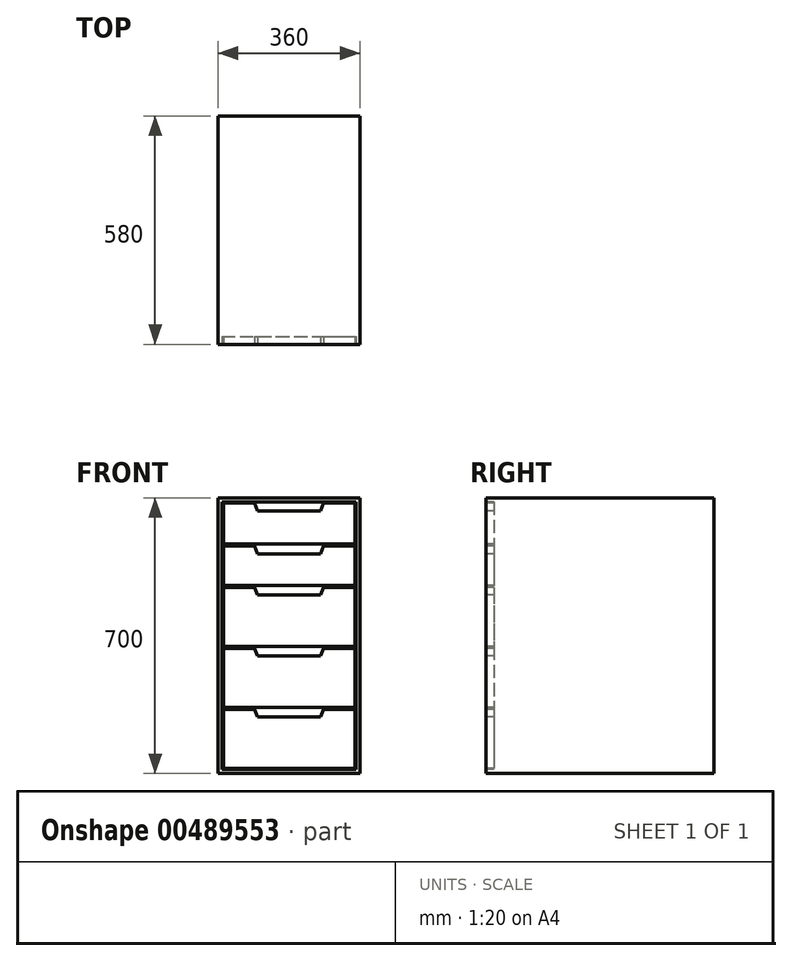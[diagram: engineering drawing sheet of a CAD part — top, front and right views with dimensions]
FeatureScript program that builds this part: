
annotation { "Feature Type Name" : "Feature", "Feature Type Description" : "" }
export const myFeature = defineFeature(function(context is Context, id is Id, definition is map)
    precondition{}
    {
        {
            var Q0;
            Q0=qCreatedBy(makeId("Top.planeOp"),FACE);
            var sketch = newSketch(context, id + "F0", { "sketchPlane" : qUnion([Q0])});
            skLineSegment(sketch, "E0.bottom", {"start": v(180, -290) * mm, "end": v(-180, -290) * mm});
            skLineSegment(sketch, "E0.top", {"start": v(180, 290) * mm, "end": v(-180, 290) * mm});
            skLineSegment(sketch, "E0.left", {"start": v(180, -290) * mm, "end": v(180, 290) * mm});
            skLineSegment(sketch, "E0.right", {"start": v(-180, -290) * mm, "end": v(-180, 290) * mm});
            skPoint(sketch, "E0.middle", {"position": v(0, 0) * mm});
            skSolve(sketch);
        }
        {
            var Q0;
            Q0 = qSketchRegion(id + "F0", true);
            extrude(context, id + "F1", {"entities" : qUnion([Q0]), "depth" : 700 * mm});
        }
        {
            var Q0;
            Q0=makeQuery(id+"F1.opExtrude","SWEPT_FACE",FACE,{"disambiguationData":[OSD([sQuery(id+"F0.wireOp",EDGE,"E0.bottom")])]});
            var sketch = newSketch(context, id + "F2", { "sketchPlane" : qUnion([Q0])});
            skLineSegment(sketch, "E1.bottom", {"start": v(-170, 690) * mm, "end": v(170, 690) * mm});
            skLineSegment(sketch, "E1.top", {"start": v(-170, 10) * mm, "end": v(170, 10) * mm});
            skLineSegment(sketch, "E1.left", {"start": v(-170, 690) * mm, "end": v(-170, 10) * mm});
            skLineSegment(sketch, "E1.right", {"start": v(170, 690) * mm, "end": v(170, 10) * mm});
            skLineSegment(sketch, "E2.top", {"start": v(-167, 13) * mm, "end": v(167, 13) * mm});
            skLineSegment(sketch, "E2.left", {"start": v(-167, 687) * mm, "end": v(-167, 583) * mm});
            skLineSegment(sketch, "E2.right", {"start": v(167, 687) * mm, "end": v(167, 583) * mm});
            skLineSegment(sketch, "E3", {"start": v(-167, 168) * mm, "end": v(167, 168) * mm});
            skLineSegment(sketch, "E4", {"start": v(-167, 478) * mm, "end": v(167, 478) * mm});
            skLineSegment(sketch, "E5", {"start": v(-167, 583) * mm, "end": v(167, 583) * mm});
            skLineSegment(sketch, "E6", {"start": v(-167, 323) * mm, "end": v(167, 323) * mm});
            skLineSegment(sketch, "E7", {"start": v(-167, 163) * mm, "end": v(-87.78, 163) * mm});
            skLineSegment(sketch, "E8", {"start": v(-87.78, 163) * mm, "end": v(-80, 143) * mm});
            skLineSegment(sketch, "E9", {"start": v(-80, 143) * mm, "end": v(80, 143) * mm});
            skLineSegment(sketch, "E10", {"start": v(80, 143) * mm, "end": v(87.78, 163) * mm});
            skLineSegment(sketch, "E11", {"start": v(87.78, 163) * mm, "end": v(167, 163) * mm});
            skLineSegment(sketch, "E12", {"start": v(-167, 318) * mm, "end": v(-87.78, 318) * mm});
            skLineSegment(sketch, "E13", {"start": v(-87.78, 318) * mm, "end": v(-80, 298) * mm});
            skLineSegment(sketch, "E14", {"start": v(-80, 298) * mm, "end": v(80, 298) * mm});
            skLineSegment(sketch, "E15", {"start": v(80, 298) * mm, "end": v(87.78, 318) * mm});
            skLineSegment(sketch, "E16", {"start": v(87.78, 318) * mm, "end": v(167, 318) * mm});
            skLineSegment(sketch, "E17", {"start": v(-167, 473) * mm, "end": v(-87.78, 473) * mm});
            skLineSegment(sketch, "E18", {"start": v(-87.78, 473) * mm, "end": v(-80, 453) * mm});
            skLineSegment(sketch, "E19", {"start": v(-80, 453) * mm, "end": v(80, 453) * mm});
            skLineSegment(sketch, "E20", {"start": v(80, 453) * mm, "end": v(87.78, 473) * mm});
            skLineSegment(sketch, "E21", {"start": v(87.78, 473) * mm, "end": v(167, 473) * mm});
            skLineSegment(sketch, "E22", {"start": v(-167, 687) * mm, "end": v(-87.78, 687) * mm});
            skLineSegment(sketch, "E23", {"start": v(-87.78, 687) * mm, "end": v(-80, 667) * mm});
            skLineSegment(sketch, "E24", {"start": v(-80, 667) * mm, "end": v(80, 667) * mm});
            skLineSegment(sketch, "E25", {"start": v(80, 667) * mm, "end": v(87.78, 687) * mm});
            skLineSegment(sketch, "E26", {"start": v(87.78, 687) * mm, "end": v(167, 687) * mm});
            skLineSegment(sketch, "E27", {"start": v(-167, 578) * mm, "end": v(-87.78, 578) * mm});
            skLineSegment(sketch, "E28", {"start": v(-87.78, 578) * mm, "end": v(-80, 558) * mm});
            skLineSegment(sketch, "E29", {"start": v(-80, 558) * mm, "end": v(80, 558) * mm});
            skLineSegment(sketch, "E30", {"start": v(80, 558) * mm, "end": v(87.78, 578) * mm});
            skLineSegment(sketch, "E31", {"start": v(87.78, 578) * mm, "end": v(167, 578) * mm});
            skLineSegment(sketch, "E32.trimOffspring", {"start": v(-167, 578) * mm, "end": v(-167, 478) * mm});
            skLineSegment(sketch, "E33.trimOffspring", {"start": v(167, 578) * mm, "end": v(167, 478) * mm});
            skLineSegment(sketch, "E34.trimOffspring", {"start": v(-167, 473) * mm, "end": v(-167, 323) * mm});
            skLineSegment(sketch, "E35.trimOffspring", {"start": v(167, 473) * mm, "end": v(167, 323) * mm});
            skLineSegment(sketch, "E36.trimOffspring", {"start": v(167, 163) * mm, "end": v(167, 13) * mm});
            skLineSegment(sketch, "E37.trimOffspring", {"start": v(167, 318) * mm, "end": v(167, 168) * mm});
            skLineSegment(sketch, "E38.trimOffspring", {"start": v(-167, 318) * mm, "end": v(-167, 168) * mm});
            skLineSegment(sketch, "E39.trimOffspring", {"start": v(-167, 163) * mm, "end": v(-167, 13) * mm});
            skLineSegment(sketch, "E40", {"start": v(0, 583) * mm, "end": v(0, 558) * mm, "construction": true});
            skLineSegment(sketch, "E41", {"start": v(0, 558) * mm, "end": v(0, 453) * mm, "construction": true});
            skPoint(sketch, "E41.endSnap0", {"position": v(0, 453) * mm});
            skLineSegment(sketch, "E42", {"start": v(0, 453) * mm, "end": v(0, 298) * mm, "construction": true});
            skPoint(sketch, "E42.endSnap0", {"position": v(0, 298) * mm});
            skLineSegment(sketch, "E43", {"start": v(0, 298) * mm, "end": v(0, 143) * mm, "construction": true});
            skLineSegment(sketch, "E44", {"start": v(0, 667) * mm, "end": v(0, 690) * mm, "construction": true});
            skSolve(sketch);
        }
        {
            var Q0;
            Q0=makeQuery(id+"F2.imprint","IMPRINT",FACE,{"disambiguationData":[TD([[makeQuery(id+"F2.imprint","IMPRINT",EDGE,{"derivedFrom":sQuery(id+"F2.wireOp",EDGE,"E1.bottom")}),-1.0]])]});
            extrude(context, id + "F3", {"entities" : qUnion([Q0]), "operationType" : NewBodyOperationType.REMOVE, "oppositeDirection" : true, "depth" : 20 * mm});
        }
    });
